# Revit family: 17. Промежуточная секция ANR Z1
name_source: partatom
category: Оборудование
revit_build: Autodesk Revit 2016 (Build: 20161004_0715(x64)
units: mm (PartAtom-declared; Revit-internal decimal feet)

## family parameters
Всегда вертикально = Да
На основе рабочей плоскости = Нет
Общий = Нет
При загрузке вырезать с полостями = Нет
Размер круглого соединителя = Использовать диаметр
Тип детали = Нормальный
Точка расчета площади = Нет

## types (10) — shared parameters
h = 130 мм
Д = 575 мм
Д1 = 555 мм
Единица измерения = шт.
Завод изготовитель = NED
Ключевая пометка = Вентиляция
Материал = Сталь серая
Наименование и тех.хар-ка = Промежуточная секция
Раздел = ОВ
Синий = Синий
высота ножек = 120 мм

## per-type parameters (varying)
| type | А | А1 | Б | Б1 | Высота | Середина | Ширина |
| ANR 6 Z1 | 1100 мм | 1080 мм | 1100 мм | 1080 мм | 1025 мм | 670 мм | 1025 мм |
| ANR 7 Z1 | 1100 мм | 1080 мм | 1320 мм | 1300 мм | 1245 мм | 780 мм | 1025 мм |
| ANR 8 Z1 | 1320 мм | 1300 мм | 1320 мм | 1300 мм | 1245 мм | 780 мм | 1245 мм |
| ANR 12 Z1 | 1435 мм | 1415 мм | 1435 мм | 1415 мм | 1360 мм | 838 мм | 1360 мм |
| ANR 20 Z1 | 1660 мм | 1640 мм | 1660 мм | 1640 мм | 1585 мм | 950 мм | 1585 мм |
| ANR 25 Z1 | 2045 мм | 2025 мм | 2045 мм | 2025 мм | 1970 мм | 1143 мм | 1970 мм |
| ANR 30 Z1 | 2485 мм | 2465 мм | 2045 мм | 2025 мм | 1970 мм | 1143 мм | 2410 мм |
| ANR 35 Z1 | 2485 мм | 2465 мм | 2485 мм | 2465 мм | 2410 мм | 1363 мм | 2410 мм |
| ANR 40 Z1 | 3320 мм | 3300 мм | 3440 мм | 3420 мм | 3365 мм | 1840 мм | 3245 мм |
| ANR 45 Z1 | 3320 мм | 3300 мм | 4210 мм | 4190 мм | 4135 мм | 2225 мм | 3245 мм |

note: column(s) folded — value = type name in every type: Тип, марка, обозначение
